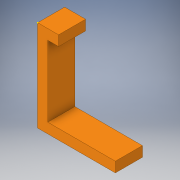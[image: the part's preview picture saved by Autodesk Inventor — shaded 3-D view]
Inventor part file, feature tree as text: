
AUTODESK INVENTOR PART (.ipt)
format: ipt  version: 2017 (Build 210142000, 142)  size: 126,464 bytes
history: native  units: in
note: dims shown in document units (in); Inventor stores cm internally (conversion verified against a paired STEP export)
features: sketch x6, extrude x5
ambient origin geometry x8: Origin, YZ Plane, XZ Plane, XY Plane, X Axis, Y Axis, Z Axis, Center Point
bodies: Solid1 (feature_tree)
feature tree (11):
  extrude  "Extrusion1"  Depth=0.375in
  extrude  "Extrusion2"  Depth=0.375in
  extrude  "Extrusion3"  Depth=1.0in
  extrude  "Extrusion4"  Depth=2.5in TaperAngle=0.0deg
  extrude  "Extrusion5"  Depth=1.0in TaperAngle=0.0deg
  sketch  "Sketch6"  dims[d14=0.375in d15=1.0in d16=0.0in]
  sketch  "Sketch1"  dims[d0=0.375in d1=3.75in]
  sketch  "Sketch2"  dims[d2=1.0in d3=0.0in d4=0.375in]
  sketch  "Sketch3"  dims[d5=0.4in d6=0.0in d7=1.0in]
  sketch  "Sketch4"  dims[d8=0.375in d9=2.5in d10=0.0in]
  sketch  "Sketch5"  dims[d11=0.375in d12=1.0in d13=0.0in]
